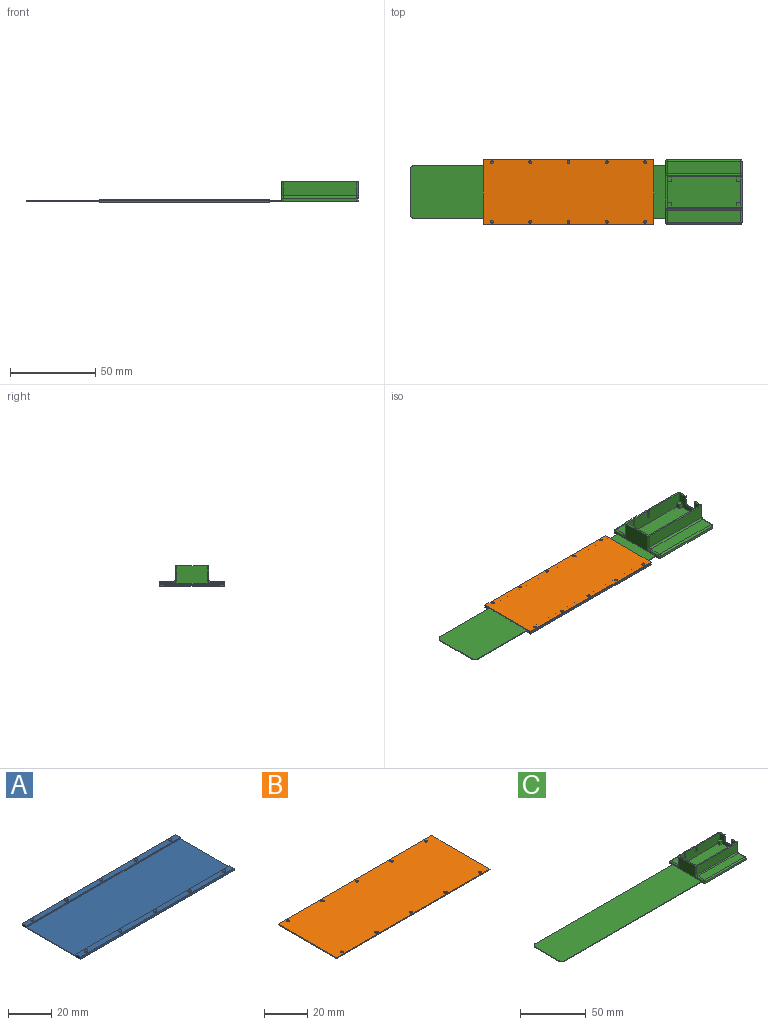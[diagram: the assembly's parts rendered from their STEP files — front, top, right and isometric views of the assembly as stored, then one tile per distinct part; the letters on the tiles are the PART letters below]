
ASSEMBLY  parts=3 mates=2
PART A: 30 faces, bbox 100x38x1.8 mm
  f0: plane 100x32mm, normal (0,0,1), area 3200mm2, adj f1,f3,f6,f8
  f1: plane 38x1.3mm, normal (1,0,0), area 23.8mm2, adj f0,f2,f4,f5,f6,f7,f8,f9
  f2: plane 100x1.3mm, normal (0,1,0), area 130mm2, adj f1,f3,f5,f7
  f3: plane 38x1.3mm, normal (-1,0,0), area 23.8mm2, adj f0,f2,f4,f5,f6,f7,f8,f9
  f4: plane 100x1.3mm, normal (0,-1,0), area 130mm2, adj f1,f3,f5,f9
  f5: plane 100x38mm, normal (0,0,-1), area 3800mm2, adj f1,f2,f3,f4
  f6: plane 100x0.8mm, normal (0,-1,0), area 80mm2, adj f0,f1,f3,f7
  f7: plane 100x3mm, normal (0,0,1), area 291.2mm2, adj f1,f2,f3,f6,f10,f12,f14,f16
  f8: plane 100x0.8mm, normal (0,1,0), area 80mm2, adj f0,f1,f3,f9
  f9: plane 100x3mm, normal (0,0,1), area 291.2mm2, adj f1,f3,f4,f8,f20,f22,f24,f26
  f10: cylinder r=0.75mm len=1.5mm, axis (0,0,-1), area 2.4mm2, adj f7,f11
  f11: plane 1.5x1.5mm, normal (0,0,1), area 1.8mm2, adj f10
  f12: cylinder r=0.75mm len=1.5mm, axis (0,0,-1), area 2.4mm2, adj f7,f13
  f13: plane 1.5x1.5mm, normal (0,0,1), area 1.8mm2, adj f12
  f14: cylinder r=0.75mm len=1.5mm, axis (0,0,-1), area 2.4mm2, adj f7,f15
  f15: plane 1.5x1.5mm, normal (0,0,1), area 1.8mm2, adj f14
  f16: cylinder r=0.75mm len=1.5mm, axis (0,0,-1), area 2.4mm2, adj f7,f17
  f17: plane 1.5x1.5mm, normal (0,0,1), area 1.8mm2, adj f16
  f18: cylinder r=0.75mm len=1.5mm, axis (0,0,-1), area 2.4mm2, adj f7,f19
  f19: plane 1.5x1.5mm, normal (0,0,1), area 1.8mm2, adj f18
  f20: cylinder r=0.75mm len=1.5mm, axis (0,0,-1), area 2.4mm2, adj f9,f21
  f21: plane 1.5x1.5mm, normal (0,0,1), area 1.8mm2, adj f20
  f22: cylinder r=0.75mm len=1.5mm, axis (0,0,-1), area 2.4mm2, adj f9,f23
  f23: plane 1.5x1.5mm, normal (0,0,1), area 1.8mm2, adj f22
  f24: cylinder r=0.75mm len=1.5mm, axis (0,0,-1), area 2.4mm2, adj f9,f25
  f25: plane 1.5x1.5mm, normal (0,0,1), area 1.8mm2, adj f24
  f26: cylinder r=0.75mm len=1.5mm, axis (0,0,-1), area 2.4mm2, adj f9,f27
  f27: plane 1.5x1.5mm, normal (0,0,1), area 1.8mm2, adj f26
  f28: cylinder r=0.75mm len=1.5mm, axis (0,0,-1), area 2.4mm2, adj f9,f29
  f29: plane 1.5x1.5mm, normal (0,0,1), area 1.8mm2, adj f28
PART B: 16 faces, bbox 100x38x0.5 mm
  f0: plane 38x0.5mm, normal (1,0,0), area 19mm2, adj f1,f3,f4,f5
  f1: plane 100x0.5mm, normal (0,1,0), area 50mm2, adj f0,f2,f4,f5
  f2: plane 38x0.5mm, normal (-1,0,0), area 19mm2, adj f1,f3,f4,f5
  f3: plane 100x0.5mm, normal (0,-1,0), area 50mm2, adj f0,f2,f4,f5
  f4: plane 100x38mm, normal (0,0,1), area 3779.9mm2, adj f0,f1,f2,f3,f6,f7,f8,f9
  f5: plane 100x38mm, normal (0,0,-1), area 3779.9mm2, adj f0,f1,f2,f3,f6,f7,f8,f9
  f6: cylinder r=0.8mm len=1.6mm, axis (0,0,1), area 2.5mm2, adj f4,f5
  f7: cylinder r=0.8mm len=1.6mm, axis (0,0,1), area 2.5mm2, adj f4,f5
  f8: cylinder r=0.8mm len=1.6mm, axis (0,0,1), area 2.5mm2, adj f4,f5
  f9: cylinder r=0.8mm len=1.6mm, axis (0,0,1), area 2.5mm2, adj f4,f5
  f10: cylinder r=0.8mm len=1.6mm, axis (0,0,1), area 2.5mm2, adj f4,f5
  f11: cylinder r=0.8mm len=1.6mm, axis (0,0,1), area 2.5mm2, adj f4,f5
  f12: cylinder r=0.8mm len=1.6mm, axis (0,0,1), area 2.5mm2, adj f4,f5
  f13: cylinder r=0.8mm len=1.6mm, axis (0,0,1), area 2.5mm2, adj f4,f5
  f14: cylinder r=0.8mm len=1.6mm, axis (0,0,1), area 2.5mm2, adj f4,f5
  f15: cylinder r=0.8mm len=1.6mm, axis (0,0,1), area 2.5mm2, adj f4,f5
PART C: 68 faces, bbox 195x38x11.5 mm
  f0: plane 10.75x1mm, normal (0,0,1), area 10.8mm2, adj f2,f4,f38,f41
  f1: plane 45x19.7mm, normal (0,0,1), area 72mm2, adj f2,f3,f4,f6,f11,f19,f20,f21
  f2: plane 43x8mm, normal (0,1,0), area 329.5mm2, adj f0,f1,f22,f38,f39,f40,f41,f42
  f3: plane 36x11.5mm, normal (1,0,0), area 185.9mm2, adj f1,f17,f22,f35,f36,f37,f50,f51
  f4: plane 43.2x9mm, normal (0,-1,0), area 359.3mm2, adj f0,f1,f5,f6,f21,f22,f24,f25
  f5: plane 43.2x17.7mm, normal (0,0,1), area 739.6mm2, adj f4,f6,f20,f21,f23,f24,f26,f27
  f6: plane 17.7x9mm, normal (-1,0,0), area 97.5mm2, adj f1,f4,f5,f20,f22,f30,f31,f33
  f7: plane 43x7.15mm, normal (0,0,1), area 307.4mm2, adj f59,f60,f64,f65
  f8: plane 147x0.5mm, normal (0,-1,0), area 73.5mm2, adj f11,f15,f16,f17
  f9: plane 43x1.5mm, normal (0,-1,0), area 64.5mm2, adj f17,f45,f51,f52
  f10: plane 43x1.5mm, normal (0,1,0), area 64.5mm2, adj f17,f56,f60,f61
  f11: plane 36x11.5mm, normal (-1,0,0), area 217mm2, adj f1,f8,f12,f16,f17,f44,f45,f46
  f12: plane 147x0.5mm, normal (0,1,0), area 73.5mm2, adj f11,f13,f16,f17
  f13: cylinder r=3mm len=3mm, axis (0,0,-1), area 2.4mm2, adj f12,f14,f16,f17
  f14: plane 25.5x0.5mm, normal (-1,0,0), area 12.8mm2, adj f13,f15,f16,f17
  f15: cylinder r=3mm len=3mm, axis (0,0,-1), area 2.4mm2, adj f8,f14,f16,f17
  f16: plane 150x31.5mm, normal (0,0,1), area 4721.1mm2, adj f8,f11,f12,f13,f14,f15
  f17: plane 195x38mm, normal (0,0,-1), area 6430.3mm2, adj f3,f8,f9,f10,f11,f12,f13,f14
  f18: plane 43x7.15mm, normal (0,0,1), area 307.4mm2, adj f46,f49,f52,f55
  f19: plane 43x8mm, normal (0,-1,0), area 344mm2, adj f1,f44,f49,f50
  f20: plane 43.2x9mm, normal (0,1,0), area 373.8mm2, adj f1,f5,f6,f21,f26,f28,f29,f31
  f21: plane 17.7x9mm, normal (1,0,0), area 144.3mm2, adj f1,f4,f5,f20,f23,f25,f27,f28
  f22: plane 25.25x5.95mm, normal (0,0,1), area 29mm2, adj f2,f3,f4,f6,f36,f40,f67
  f23: plane 3x2.5mm, normal (0,-1,0), area 7.5mm2, adj f5,f21,f24,f25
  f24: plane 3x2.5mm, normal (1,0,0), area 7.5mm2, adj f4,f5,f23,f25
  f25: plane 2.5x2.5mm, normal (0,0,1), area 6.2mm2, adj f4,f21,f23,f24
  f26: plane 3x2.5mm, normal (1,0,0), area 7.5mm2, adj f5,f20,f27,f28
  f27: plane 3x2.5mm, normal (0,1,0), area 7.5mm2, adj f5,f21,f26,f28
  f28: plane 2.5x2.5mm, normal (0,0,1), area 6.2mm2, adj f20,f21,f26,f27
  f29: plane 3x2.5mm, normal (-1,0,0), area 7.5mm2, adj f5,f20,f30,f31
  f30: plane 3x2.5mm, normal (0,1,0), area 7.5mm2, adj f5,f6,f29,f31
  f31: plane 2.5x2.5mm, normal (0,0,1), area 6.3mm2, adj f6,f20,f29,f30
  f32: plane 3x2.5mm, normal (-1,0,0), area 7.5mm2, adj f4,f5,f33,f34
  f33: plane 3x2.5mm, normal (0,-1,0), area 7.5mm2, adj f5,f6,f32,f34
  f34: plane 2.5x2.5mm, normal (0,0,1), area 6.3mm2, adj f4,f6,f32,f33
  f35: plane 6x0.8mm, normal (0,1,0), area 4.8mm2, adj f1,f3,f6,f37
  f36: plane 6x0.8mm, normal (0,-1,0), area 4.8mm2, adj f3,f6,f22,f37
  f37: plane 7.8x0.8mm, normal (0,0,1), area 6.2mm2, adj f3,f6,f35,f36
  f38: plane 4.26x1mm, normal (-1,0,0), area 4.3mm2, adj f0,f2,f4,f42
  f39: plane 4.26x1mm, normal (1,0,0), area 4.3mm2, adj f1,f2,f4,f42
  f40: plane 4.25x1mm, normal (-1,0,0), area 4.3mm2, adj f2,f4,f22,f43
  f41: plane 4.25x1mm, normal (1,0,0), area 4.3mm2, adj f0,f2,f4,f43
  f42: cylinder r=0.75mm len=1.5mm, axis (0,-1,0), area 2.4mm2, adj f2,f4,f38,f39
  f43: cylinder r=0.75mm len=1.5mm, axis (0,-1,0), area 2.4mm2, adj f2,f4,f40,f41
  f44: cylinder r=1mm len=8mm, axis (0,0,-1), area 12.6mm2, adj f1,f11,f19,f47
  f45: cylinder r=1mm len=1.5mm, axis (0,0,-1), area 2.4mm2, adj f9,f11,f17,f48
  f46: cylinder r=1mm len=7.15mm, axis (0,1,0), area 11.2mm2, adj f11,f18,f47,f48
  f47: torus R=2mm, axis (1,0,0), area 3.4mm2, adj f11,f44,f46,f49
  f48: sphere r=1mm, area 1.6mm2, adj f45,f46,f52
  f49: cylinder r=1mm len=43mm, axis (1,0,0), area 67.5mm2, adj f18,f19,f47,f53
  f50: cylinder r=1mm len=8mm, axis (0,0,1), area 12.6mm2, adj f1,f3,f19,f53
  f51: cylinder r=1mm len=1.5mm, axis (0,0,1), area 2.4mm2, adj f3,f9,f17,f54
  f52: cylinder r=1mm len=43mm, axis (-1,0,0), area 67.5mm2, adj f9,f18,f48,f54
  f53: torus R=2mm, axis (1,0,0), area 3.4mm2, adj f3,f49,f50,f55
  f54: sphere r=1mm, area 1.6mm2, adj f51,f52,f55
  f55: cylinder r=1mm len=7.15mm, axis (0,-1,0), area 11.2mm2, adj f3,f18,f53,f54
  f56: cylinder r=1mm len=1.5mm, axis (0,0,1), area 2.4mm2, adj f10,f11,f17,f57
  f57: sphere r=1mm, area 1.6mm2, adj f56,f59,f60
  f58: cylinder r=1mm len=8mm, axis (0,0,1), area 12.6mm2, adj f1,f2,f11,f62
  f59: cylinder r=1mm len=7.15mm, axis (0,1,0), area 11.2mm2, adj f7,f11,f57,f62
  f60: cylinder r=1mm len=43mm, axis (1,0,0), area 67.5mm2, adj f7,f10,f57,f63
  f61: cylinder r=1mm len=1.5mm, axis (0,0,-1), area 2.4mm2, adj f3,f10,f17,f63
  f62: torus R=2mm, axis (1,0,0), area 3.4mm2, adj f11,f58,f59,f64
  f63: sphere r=1mm, area 1.6mm2, adj f60,f61,f65
  f64: cylinder r=1mm len=43mm, axis (-1,0,0), area 67.5mm2, adj f2,f7,f62,f66
  f65: cylinder r=1mm len=7.15mm, axis (0,-1,0), area 11.2mm2, adj f3,f7,f63,f66
  f66: torus R=2mm, axis (1,0,0), area 3.4mm2, adj f3,f64,f65,f67
  f67: cylinder r=1mm len=8mm, axis (0,0,-1), area 12.6mm2, adj f2,f3,f22,f66
PLACE A rot(axis=(0,0,-1),180deg) t=(-122.17,29.05,-134.37)mm
PLACE B rot(axis=(1,0,0),180deg) t=(-22.17,29.05,-133.07)mm
PLACE C t=(-15.29,29.05,-134.37)mm
MATE fastened B.f15 <-> A.f18  axis (0,0,1) through (-117.17,11.55,-133.07)mm
MATE slider A.f3 <-> C.f11  axis (-1,0,0) through (-22.17,29.05,-134.37)mm
